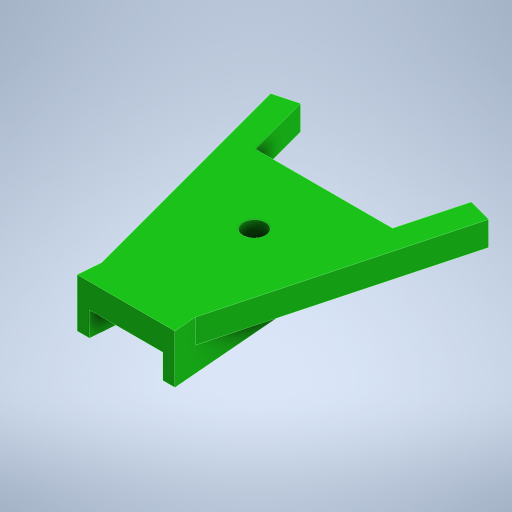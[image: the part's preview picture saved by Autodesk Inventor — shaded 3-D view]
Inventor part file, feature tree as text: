
AUTODESK INVENTOR PART (.ipt)
format: ipt  version: 2023 (Build 270158000, 158)  size: 296,448 bytes
history: native  units: mm
features: extrude x2, sketch x1
ambient origin geometry x8: Origin, YZ Plane, XZ Plane, XY Plane, X Axis, Y Axis, Z Axis, Center Point
bodies: Solid1 (feature_tree)
feature tree (3):
  sketch  "Sketch1"  dims[d0=1.0mm d1=2.0mm d2=1.5mm d3=2.0mm d4=2.0mm d5=1.0mm d6=1.0mm d10=1.25mm d13=4.3mm d16=27.0mm d25=2.0mm d26=0.0mm d41=2.0mm d42=1.0mm d43=4.0mm d44=0.5mm d45=1.0mm d46=1.85mm d47=3.0mm d48=6.0mm d49=15.0mm d61=2.0mm d62=4.0mm d63=1.0mm d64=1.0mm d65=1.0mm d66=1.0mm d67=2.0mm d68=0.0mm d69=2.0mm d70=27.0mm d71=27.0mm d72=2.0mm d73=2.0mm d75=2.0mm d76=2.0mm d77=6.0mm]
  extrude  "Extrusion1"  Depth=2.0mm
  extrude  "Extrusion2"  Depth=2.0mm
